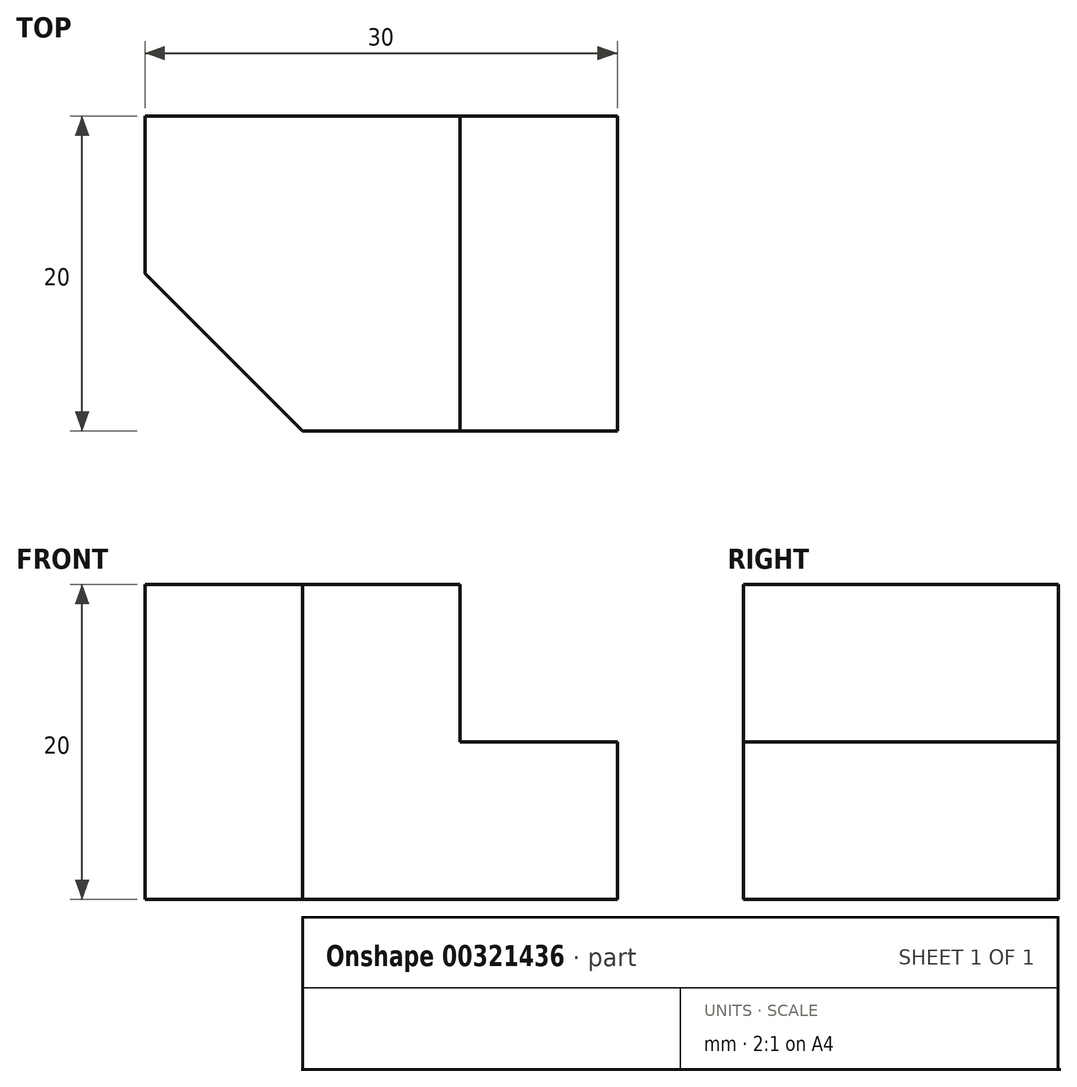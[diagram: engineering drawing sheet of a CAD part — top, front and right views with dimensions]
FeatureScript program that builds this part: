
annotation { "Feature Type Name" : "Feature", "Feature Type Description" : "" }
export const myFeature = defineFeature(function(context is Context, id is Id, definition is map)
    precondition{}
    {
        {
            var Q0;
            Q0=qCreatedBy(makeId("Front.planeOp"),FACE);
            var sketch = newSketch(context, id + "F0", { "sketchPlane" : qUnion([Q0])});
            skLineSegment(sketch, "E0.bottom", {"start": v(0, 0) * mm, "end": v(30, 0) * mm});
            skLineSegment(sketch, "E0.top", {"start": v(0, 20) * mm, "end": v(30, 20) * mm});
            skLineSegment(sketch, "E0.left", {"start": v(0, 0) * mm, "end": v(0, 20) * mm});
            skLineSegment(sketch, "E0.right", {"start": v(30, 0) * mm, "end": v(30, 20) * mm});
            skSolve(sketch);
        }
        {
            var Q0;
            Q0 = qSketchRegion(id + "F0", true);
            extrude(context, id + "F1", {"entities" : qUnion([Q0]), "depth" : 20 * mm});
        }
        {
            var Q0;
            Q0=qCreatedBy(makeId("Front.planeOp"),FACE);
            var sketch = newSketch(context, id + "F2", { "sketchPlane" : qUnion([Q0])});
            skLineSegment(sketch, "E1.bottom", {"start": v(20, 20) * mm, "end": v(30, 20) * mm});
            skLineSegment(sketch, "E1.top", {"start": v(20, 10) * mm, "end": v(30, 10) * mm});
            skLineSegment(sketch, "E1.left", {"start": v(20, 20) * mm, "end": v(20, 10) * mm});
            skLineSegment(sketch, "E1.right", {"start": v(30, 20) * mm, "end": v(30, 10) * mm});
            skSolve(sketch);
        }
        {
            var Q0;
            Q0 = qSketchRegion(id + "F2", true);
            extrude(context, id + "F3", {"entities" : qUnion([Q0]), "operationType" : NewBodyOperationType.REMOVE, "endBound" : BoundingType.THROUGH_ALL, "depth" : 25 * mm});
        }
        {
            var Q0;
            Q0=qCreatedBy(makeId("Top.planeOp"),FACE);
            var sketch = newSketch(context, id + "F4", { "sketchPlane" : qUnion([Q0])});
            skLineSegment(sketch, "E2", {"start": v(0, -10) * mm, "end": v(0, -20) * mm});
            skLineSegment(sketch, "E3", {"start": v(0, -20) * mm, "end": v(10, -20) * mm});
            skLineSegment(sketch, "E4", {"start": v(10, -20) * mm, "end": v(0, -10) * mm});
            skSolve(sketch);
        }
        {
            var Q0;
            Q0 = qSketchRegion(id + "F4", true);
            extrude(context, id + "F5", {"entities" : qUnion([Q0]), "operationType" : NewBodyOperationType.REMOVE, "endBound" : BoundingType.THROUGH_ALL, "depth" : 25 * mm});
        }
    });
